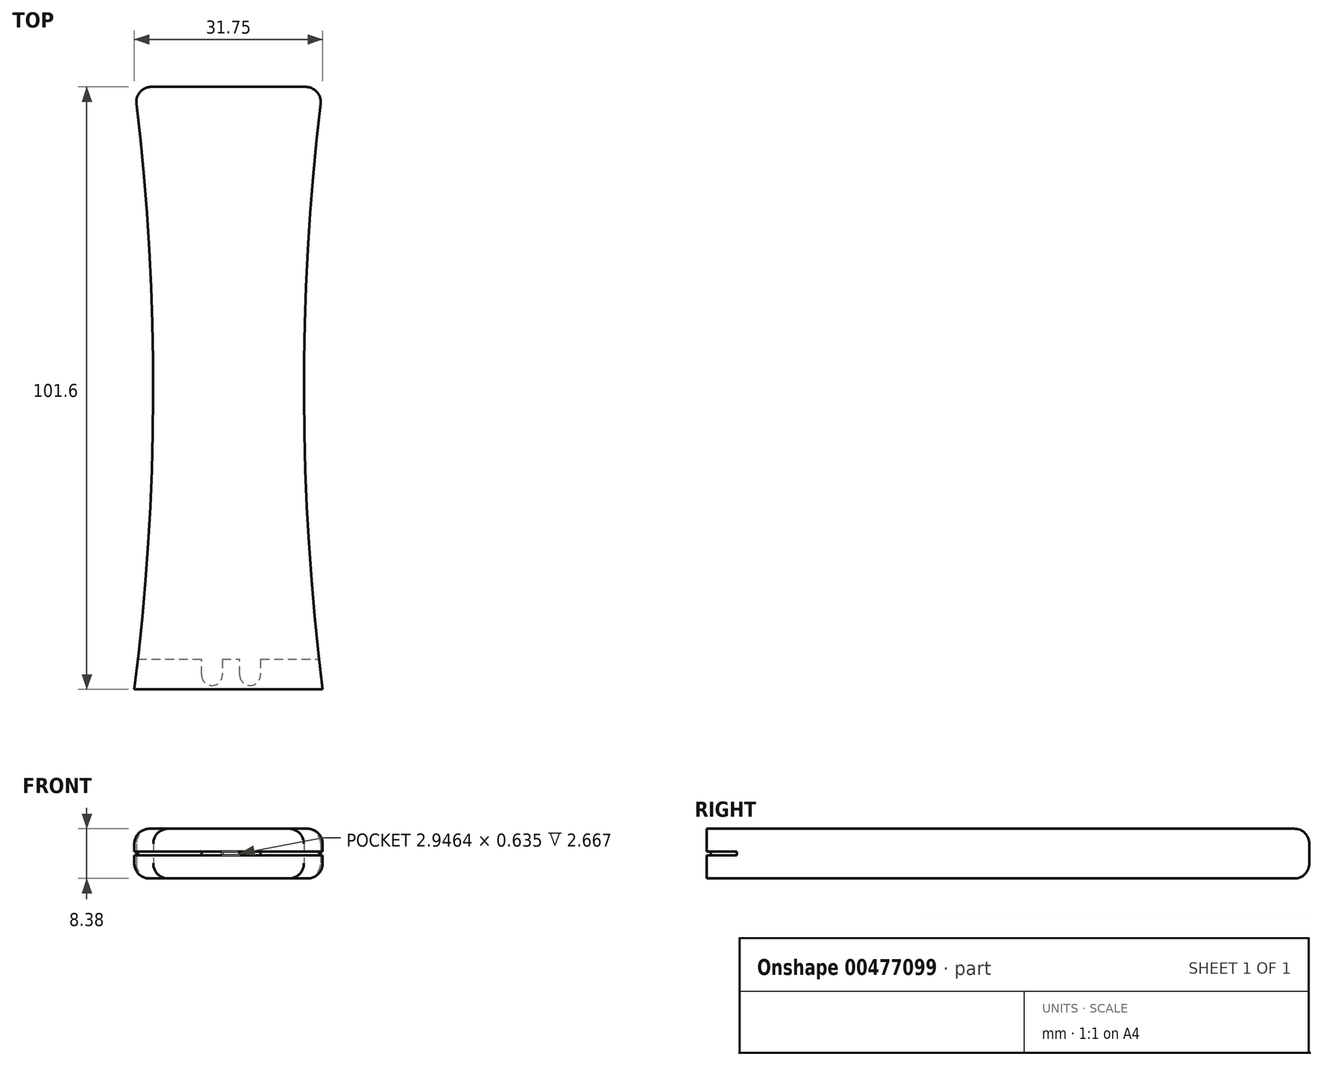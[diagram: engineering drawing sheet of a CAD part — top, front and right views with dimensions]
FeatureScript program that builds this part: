
annotation { "Feature Type Name" : "Feature", "Feature Type Description" : "" }
export const myFeature = defineFeature(function(context is Context, id is Id, definition is map)
    precondition{}
    {
        {
            var Q0;
            Q0=qCreatedBy(makeId("Top.planeOp"),FACE);
            var sketch = newSketch(context, id + "F0", { "sketchPlane" : qUnion([Q0])});
            skLineSegment(sketch, "E0.bottom", {"start": v(0, 0) * mm, "end": v(31.75, 0) * mm, "construction": true});
            skLineSegment(sketch, "E0.top", {"start": v(0, 101.6) * mm, "end": v(31.75, 101.6) * mm});
            skLineSegment(sketch, "E0.left", {"start": v(0, 0) * mm, "end": v(0, 101.6) * mm, "construction": true});
            skLineSegment(sketch, "E0.right", {"start": v(31.75, 0) * mm, "end": v(31.75, 101.6) * mm, "construction": true});
            skArc(sketch, "E1", {"start": v(0, 0) * mm, "mid": v(3.19, 50.8) * mm, "end": v(0, 101.6) * mm});
            skArc(sketch, "E2", {"start": v(31.75, 101.6) * mm, "mid": v(28.59, 50.8) * mm, "end": v(31.75, 0) * mm});
            skLineSegment(sketch, "E3", {"start": v(0, 50.8) * mm, "end": v(3.19, 50.8) * mm, "construction": true});
            skLineSegment(sketch, "E4", {"start": v(31.75, 50.8) * mm, "end": v(28.59, 50.8) * mm, "construction": true});
            skLineSegment(sketch, "E5", {"start": v(0, 0) * mm, "end": v(10.95, 0) * mm});
            skLineSegment(sketch, "E6", {"start": v(20.8, 0) * mm, "end": v(31.75, 0) * mm});
            skLineSegment(sketch, "E7", {"start": v(14.4, 0) * mm, "end": v(17.35, 0) * mm});
            skLineSegment(sketch, "E8", {"start": v(10.95, 0) * mm, "end": v(14.4, 0) * mm});
            skLineSegment(sketch, "E9", {"start": v(17.35, 0) * mm, "end": v(20.8, 0) * mm});
            skSolve(sketch);
        }
        {
            var Q0;
            Q0=makeQuery(id+"F0.imprint","IMPRINT",FACE,{"disambiguationData":[TD([[makeQuery(id+"F0.imprint","IMPRINT",EDGE,{"derivedFrom":sQuery(id+"F0.wireOp",EDGE,"E1")}),-1.0]])]});
            extrude(context, id + "F1", {"entities" : qUnion([Q0]), "depth" : 8.38 * mm});
        }
        {
            var Q0;
            Q0=makeQuery(id+"F1.opExtrude","SWEPT_FACE",FACE,{"disambiguationData":[OSD([sQuery(id+"F0.wireOp",EDGE,"E5")])]});
            var sketch = newSketch(context, id + "F2", { "sketchPlane" : qUnion([Q0])});
            skLineSegment(sketch, "E10.bottom", {"start": v(0, 3.87) * mm, "end": v(31.75, 3.87) * mm});
            skLineSegment(sketch, "E10.top", {"start": v(0, 4.5) * mm, "end": v(31.75, 4.5) * mm});
            skLineSegment(sketch, "E10.left", {"start": v(0, 3.87) * mm, "end": v(0, 4.5) * mm});
            skLineSegment(sketch, "E10.right", {"start": v(31.75, 3.87) * mm, "end": v(31.75, 4.5) * mm});
            skLineSegment(sketch, "E11", {"start": v(0, 4.2) * mm, "end": v(31.75, 4.2) * mm, "construction": true});
            skSolve(sketch);
        }
        {
            var Q0;
            Q0=makeQuery(id+"F2.imprint","IMPRINT",FACE,{"disambiguationData":[TD([[makeQuery(id+"F2.imprint","IMPRINT",EDGE,{"derivedFrom":sQuery(id+"F2.wireOp",EDGE,"E10.bottom")}),1.0]])]});
            extrude(context, id + "F3", {"entities" : qUnion([Q0]), "operationType" : NewBodyOperationType.REMOVE, "oppositeDirection" : true, "depth" : 5.08 * mm});
        }
        {
            var Q0;
            Q0=makeQuery(id+"F1.opExtrude","CAP_FACE",FACE,{"disambiguationData":[OSD([sQuery(id+"F0.wireOp",EDGE,"E1"),sQuery(id+"F0.wireOp",EDGE,"E2"),sQuery(id+"F0.wireOp",EDGE,"t2u3qaNP-rbBg-1lCq-nUBl-GO09sGmmeMCH"),sQuery(id+"F0.wireOp",EDGE,"E5"),sQuery(id+"F0.wireOp",EDGE,"E6"),sQuery(id+"F0.wireOp",EDGE,"E7"),sQuery(id+"F0.wireOp",EDGE,"E8"),sQuery(id+"F0.wireOp",EDGE,"E9")])],"isStart":false});
            var sketch = newSketch(context, id + "F4", { "sketchPlane" : qUnion([Q0])});
            skLineSegment(sketch, "E12", {"start": v(0.6, 5.08) * mm, "end": v(31.15, 5.08) * mm, "construction": true});
            skLineSegment(sketch, "E13", {"start": v(11.32, 5.08) * mm, "end": v(11.32, 2.41) * mm});
            skLineSegment(sketch, "E14", {"start": v(11.32, 2.41) * mm, "end": v(14.83, 2.41) * mm, "construction": true});
            skLineSegment(sketch, "E15", {"start": v(14.83, 2.41) * mm, "end": v(14.83, 5.08) * mm});
            skLineSegment(sketch, "E16", {"start": v(14.83, 5.08) * mm, "end": v(17.77, 5.08) * mm});
            skLineSegment(sketch, "E17", {"start": v(17.77, 5.08) * mm, "end": v(17.77, 2.41) * mm});
            skLineSegment(sketch, "E18", {"start": v(17.77, 2.41) * mm, "end": v(21.28, 2.41) * mm, "construction": true});
            skLineSegment(sketch, "E19", {"start": v(21.28, 2.41) * mm, "end": v(21.28, 5.08) * mm});
            skLineSegment(sketch, "E20", {"start": v(21.28, 5.08) * mm, "end": v(17.77, 5.08) * mm});
            skLineSegment(sketch, "E21", {"start": v(14.83, 5.08) * mm, "end": v(11.32, 5.08) * mm});
            skArc(sketch, "E22", {"start": v(11.32, 2.41) * mm, "mid": v(13.07, 0.66) * mm, "end": v(14.83, 2.41) * mm});
            skArc(sketch, "E23", {"start": v(17.77, 2.41) * mm, "mid": v(19.53, 0.66) * mm, "end": v(21.28, 2.41) * mm});
            skSolve(sketch);
        }
        {
            var Q0;
            Q0=makeQuery(id+"F4.imprint","IMPRINT",FACE,{"disambiguationData":[TD([[makeQuery(id+"F4.imprint","IMPRINT",EDGE,{"derivedFrom":sQuery(id+"F4.wireOp",EDGE,"E13")}),1.0]])]});
            var Q1;
            Q1=makeQuery(id+"F4.imprint","IMPRINT",FACE,{"disambiguationData":[TD([[makeQuery(id+"F4.imprint","IMPRINT",EDGE,{"derivedFrom":sQuery(id+"F4.wireOp",EDGE,"E17")}),1.0]])]});
            extrude(context, id + "F5", {"entities" : qUnion([Q0, Q1]), "operationType" : NewBodyOperationType.ADD, "oppositeDirection" : true, "depth" : 8.38 * mm});
        }
        {
            var Q0;
            Q0=makeQuery(id+"F1.opExtrude","SWEPT_EDGE",EDGE,{"disambiguationData":[OSD([sQuery(id+"F0.wireOp",EDGE,"E0.top"),sQuery(id+"F0.wireOp",EDGE,"E1")])]});
            var Q1;
            Q1=makeQuery(id+"F1.opExtrude","SWEPT_EDGE",EDGE,{"disambiguationData":[OSD([sQuery(id+"F0.wireOp",EDGE,"E0.top"),sQuery(id+"F0.wireOp",EDGE,"E2")])]});
            fillet(context, id + "F6", {"entities" : qUnion([Q0, Q1]), "radius" : 2.54 * mm, "tangentPropagation" : true, "allowEdgeOverflow" : false});
        }
        {
            var Q0;
            Q0=makeQuery(id+"F1.opExtrude","CAP_EDGE",EDGE,{"disambiguationData":[OSD([sQuery(id+"F0.wireOp",EDGE,"E2")])],"isStart":true});
            var Q1;
            Q1=makeQuery(id+"F1.opExtrude","CAP_EDGE",EDGE,{"disambiguationData":[OSD([sQuery(id+"F0.wireOp",EDGE,"E2")])],"isStart":false});
            fillet(context, id + "F7", {"entities" : qUnion([Q0, Q1]), "radius" : 2.54 * mm, "tangentPropagation" : true, "allowEdgeOverflow" : false});
        }
    });
